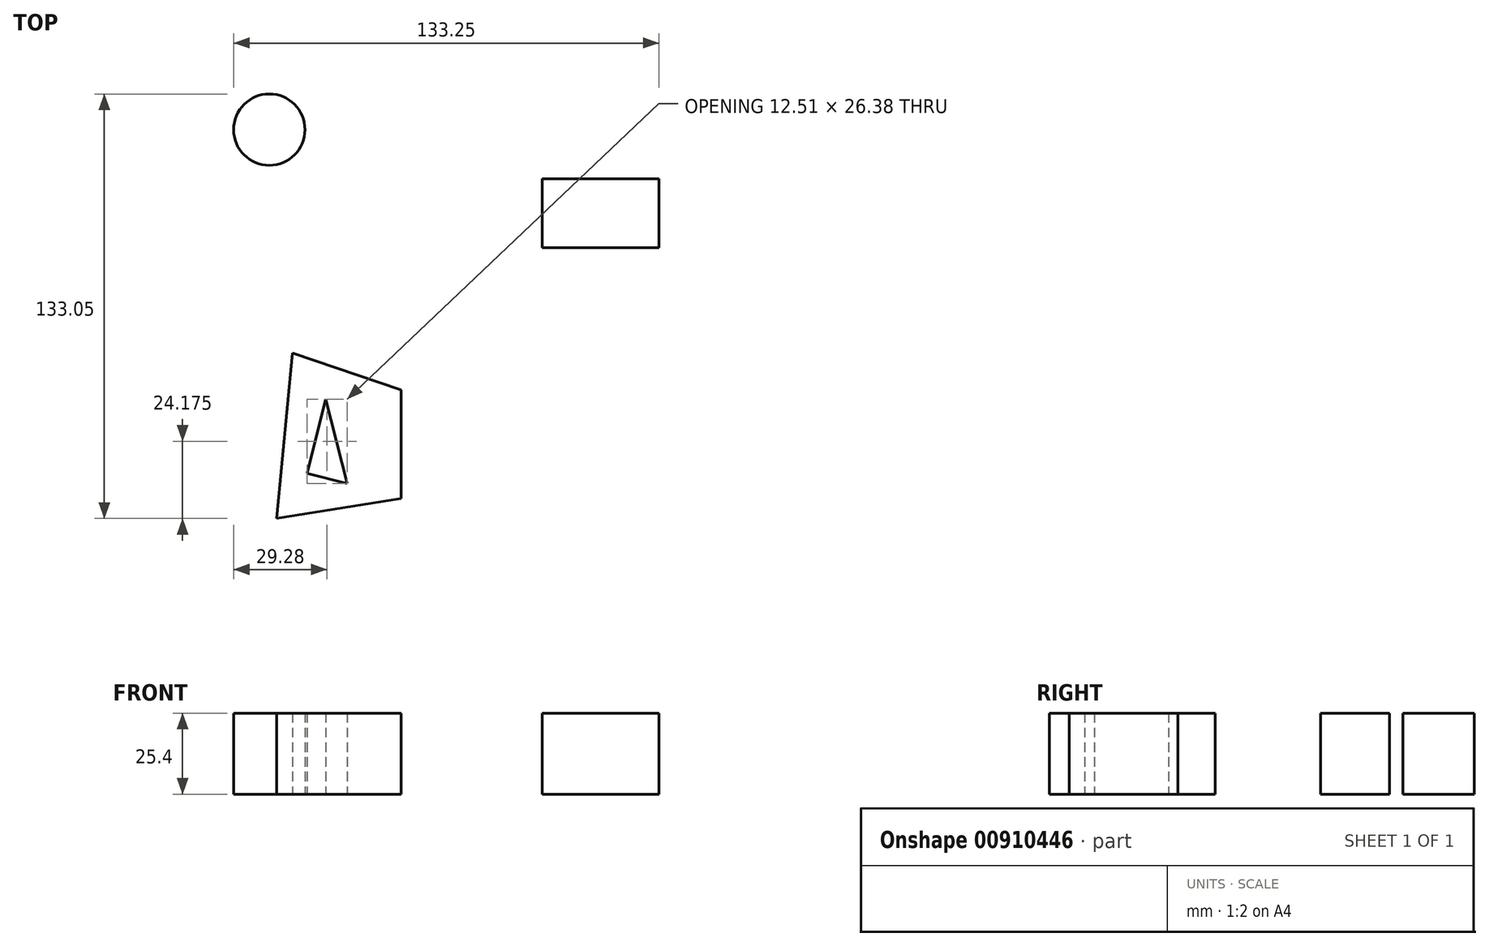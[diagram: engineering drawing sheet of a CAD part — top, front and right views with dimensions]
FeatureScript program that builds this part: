
annotation { "Feature Type Name" : "Feature", "Feature Type Description" : "" }
export const myFeature = defineFeature(function(context is Context, id is Id, definition is map)
    precondition{}
    {
        {
            var Q0;
            Q0=qCreatedBy(makeId("Top.planeOp"),FACE);
            var sketch = newSketch(context, id + "F0", { "sketchPlane" : qUnion([Q0])});
            skCircle(sketch, "E0", {"center": v(-62.28, 52.52) * mm, "radius": 11.18 * mm});
            skLineSegment(sketch, "E1.bottom", {"start": v(23.25, 37.16) * mm, "end": v(59.79, 37.16) * mm});
            skLineSegment(sketch, "E1.top", {"start": v(23.25, 15.57) * mm, "end": v(59.79, 15.57) * mm});
            skLineSegment(sketch, "E1.left", {"start": v(23.25, 37.16) * mm, "end": v(23.25, 15.57) * mm});
            skLineSegment(sketch, "E1.right", {"start": v(59.79, 37.16) * mm, "end": v(59.79, 15.57) * mm});
            skLineSegment(sketch, "E2", {"start": v(-55, -17.45) * mm, "end": v(-20.95, -29.08) * mm});
            skLineSegment(sketch, "E3", {"start": v(-20.95, -29.08) * mm, "end": v(-20.95, -63.13) * mm});
            skLineSegment(sketch, "E4", {"start": v(-20.95, -63.13) * mm, "end": v(-59.98, -69.35) * mm});
            skLineSegment(sketch, "E5", {"start": v(-59.98, -69.35) * mm, "end": v(-55, -17.45) * mm});
            skLineSegment(sketch, "E6", {"start": v(-44.62, -31.99) * mm, "end": v(-50.43, -55.24) * mm});
            skLineSegment(sketch, "E7", {"start": v(-50.43, -55.24) * mm, "end": v(-37.93, -58.36) * mm});
            skLineSegment(sketch, "E8", {"start": v(-37.93, -58.36) * mm, "end": v(-44.62, -31.99) * mm});
            skLineSegment(sketch, "E9", {"start": v(-82.91, 71.7) * mm, "end": v(-82.91, 30.26) * mm, "construction": true});
            skSolve(sketch);
        }
        {
            var Q0;
            Q0=makeQuery(id+"F0.imprint","IMPRINT",FACE,{"disambiguationData":[TD([[makeQuery(id+"F0.imprint","IMPRINT",EDGE,{"derivedFrom":sQuery(id+"F0.wireOp",EDGE,"E2")}),-1.0]])]});
            extrude(context, id + "F1", {"entities" : qUnion([Q0]), "depth" : 25.4 * mm, "offsetDistance" : 25.4 * mm});
        }
        {
            var Q0;
            Q0=makeQuery(id+"F0.imprint","IMPRINT",FACE,{"disambiguationData":[TD([[makeQuery(id+"F0.imprint","IMPRINT",EDGE,{"derivedFrom":sQuery(id+"F0.wireOp",EDGE,"E0")}),1.0]])]});
            extrude(context, id + "F2", {"entities" : qUnion([Q0]), "depth" : 25.4 * mm, "offsetDistance" : 25.4 * mm});
        }
        {
            var Q0;
            Q0=makeQuery(id+"F0.imprint","IMPRINT",FACE,{"disambiguationData":[TD([[makeQuery(id+"F0.imprint","IMPRINT",EDGE,{"derivedFrom":sQuery(id+"F0.wireOp",EDGE,"E1.bottom")}),-1.0]])]});
            extrude(context, id + "F3", {"entities" : qUnion([Q0]), "depth" : 25.4 * mm, "offsetDistance" : 25.4 * mm});
        }
    });
